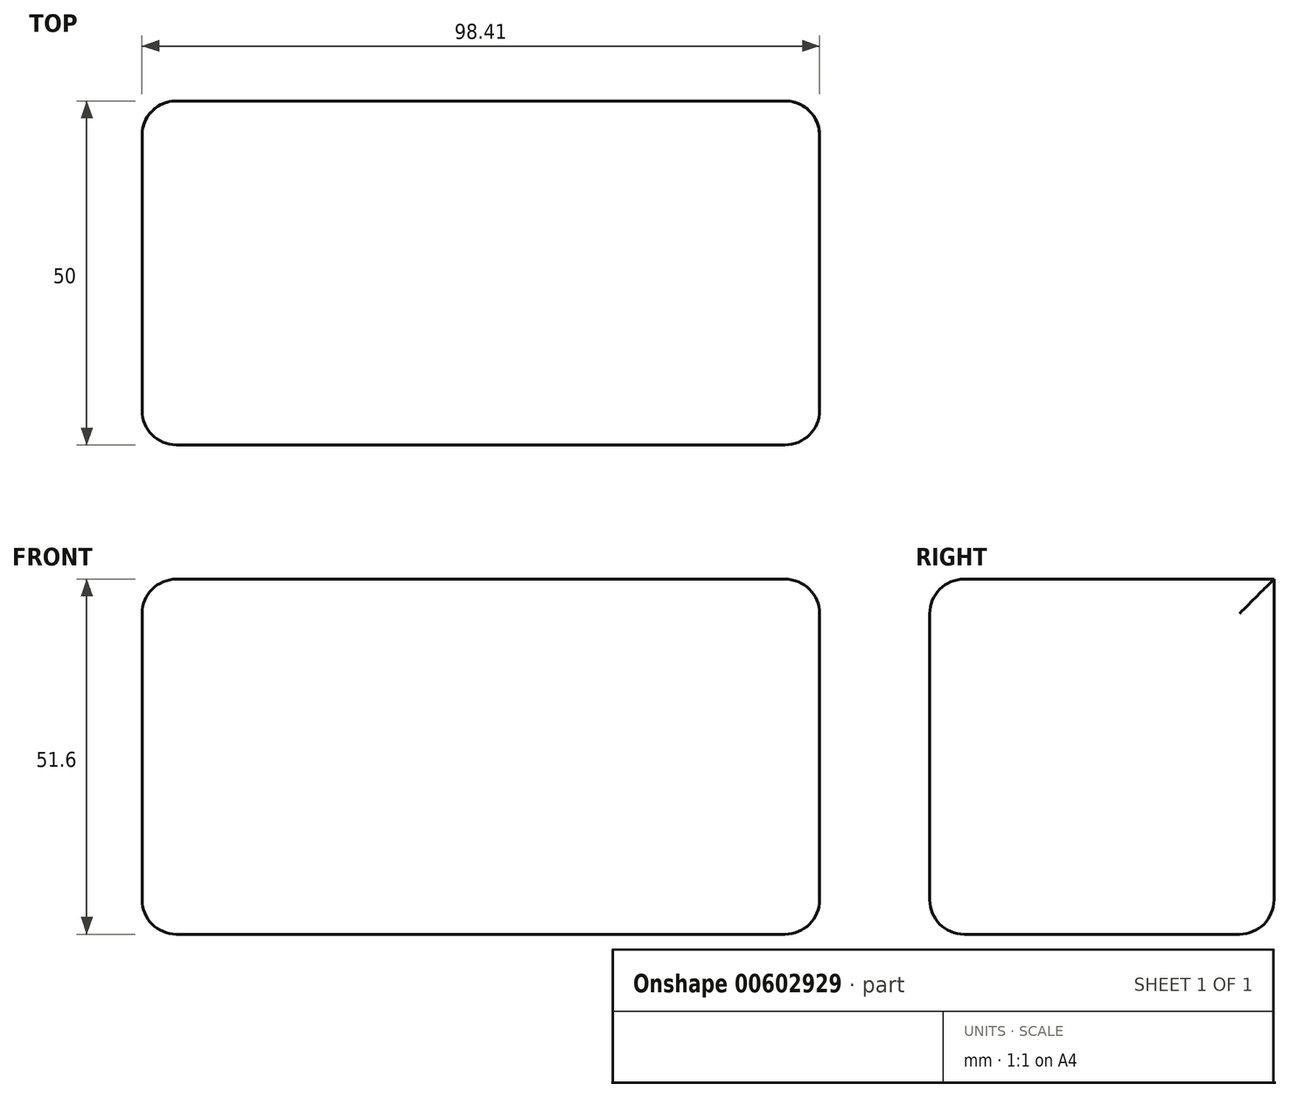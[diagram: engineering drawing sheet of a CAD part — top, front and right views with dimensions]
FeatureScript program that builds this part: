
annotation { "Feature Type Name" : "Feature", "Feature Type Description" : "" }
export const myFeature = defineFeature(function(context is Context, id is Id, definition is map)
    precondition{}
    {
        {
            var Q0;
            Q0=qCreatedBy(makeId("Front.planeOp"),FACE);
            var sketch = newSketch(context, id + "F0", { "sketchPlane" : qUnion([Q0])});
            skPoint(sketch, "E0.middle", {"position": v(0, 0) * mm});
            skLineSegment(sketch, "E1.bottom", {"start": v(0, 0) * mm, "end": v(-98.4, 0) * mm});
            skLineSegment(sketch, "E1.top", {"start": v(0, 51.6) * mm, "end": v(-98.4, 51.6) * mm});
            skLineSegment(sketch, "E1.left", {"start": v(0, 0) * mm, "end": v(0, 51.6) * mm});
            skLineSegment(sketch, "E1.right", {"start": v(-98.4, 0) * mm, "end": v(-98.4, 51.6) * mm});
            skSolve(sketch);
        }
        {
            var Q0;
            Q0 = qSketchRegion(id + "F0", true);
            extrude(context, id + "F1", {"entities" : qUnion([Q0]), "endBound" : BoundingType.SYMMETRIC, "depth" : 50 * mm, "offsetDistance" : 25 * mm});
        }
        {
            var Q0;
            Q0=makeQuery(id+"F1.opExtrude","CAP_EDGE",EDGE,{"disambiguationData":[OSD([sQuery(id+"F0.wireOp",EDGE,"E1.left")])],"isStart":false});
            var Q1;
            Q1=makeQuery(id+"F1.opExtrude","SWEPT_EDGE",EDGE,{"disambiguationData":[OSD([sQuery(id+"F0.wireOp",EDGE,"E1.top"),sQuery(id+"F0.wireOp",EDGE,"E1.left")])]});
            var Q2;
            Q2=makeQuery(id+"F1.opExtrude","CAP_EDGE",EDGE,{"disambiguationData":[OSD([sQuery(id+"F0.wireOp",EDGE,"E1.left")])],"isStart":true});
            var Q3;
            Q3=makeQuery(id+"F1.opExtrude","CAP_EDGE",EDGE,{"disambiguationData":[OSD([sQuery(id+"F0.wireOp",EDGE,"E1.top")])],"isStart":false});
            var Q4;
            Q4=makeQuery(id+"F1.opExtrude","CAP_FACE",FACE,{"disambiguationData":[OSD([sQuery(id+"F0.wireOp",EDGE,"E1.bottom"),sQuery(id+"F0.wireOp",EDGE,"E1.top"),sQuery(id+"F0.wireOp",EDGE,"E1.left"),sQuery(id+"F0.wireOp",EDGE,"E1.right")])],"isStart":false});
            fillet(context, id + "F2", {"entities" : qUnion([Q0, Q1, Q2, Q3, Q4]), "radius" : 5 * mm, "tangentPropagation" : true, "allowEdgeOverflow" : false});
        }
        {
            var Q0;
            Q0=makeQuery(id+"F1.opExtrude","CAP_EDGE",EDGE,{"disambiguationData":[OSD([sQuery(id+"F0.wireOp",EDGE,"E1.right")])],"isStart":true});
            var Q1;
            Q1=makeQuery(id+"F1.opExtrude","SWEPT_EDGE",EDGE,{"disambiguationData":[OSD([sQuery(id+"F0.wireOp",EDGE,"E1.top"),sQuery(id+"F0.wireOp",EDGE,"E1.right")])]});
            var Q2;
            Q2=makeQuery(id+"F1.opExtrude","SWEPT_EDGE",EDGE,{"disambiguationData":[OSD([sQuery(id+"F0.wireOp",EDGE,"E1.bottom"),sQuery(id+"F0.wireOp",EDGE,"E1.right")])]});
            fillet(context, id + "F3", {"entities" : qUnion([Q0, Q1, Q2]), "radius" : 5 * mm, "tangentPropagation" : true, "allowEdgeOverflow" : false});
        }
        {
            var Q0;
            Q0=makeQuery(id+"F1.opExtrude","SWEPT_EDGE",EDGE,{"disambiguationData":[OSD([sQuery(id+"F0.wireOp",EDGE,"E1.bottom"),sQuery(id+"F0.wireOp",EDGE,"E1.left")])]});
            fillet(context, id + "F4", {"entities" : qUnion([Q0]), "radius" : 5 * mm, "tangentPropagation" : true, "allowEdgeOverflow" : false});
        }
    });
